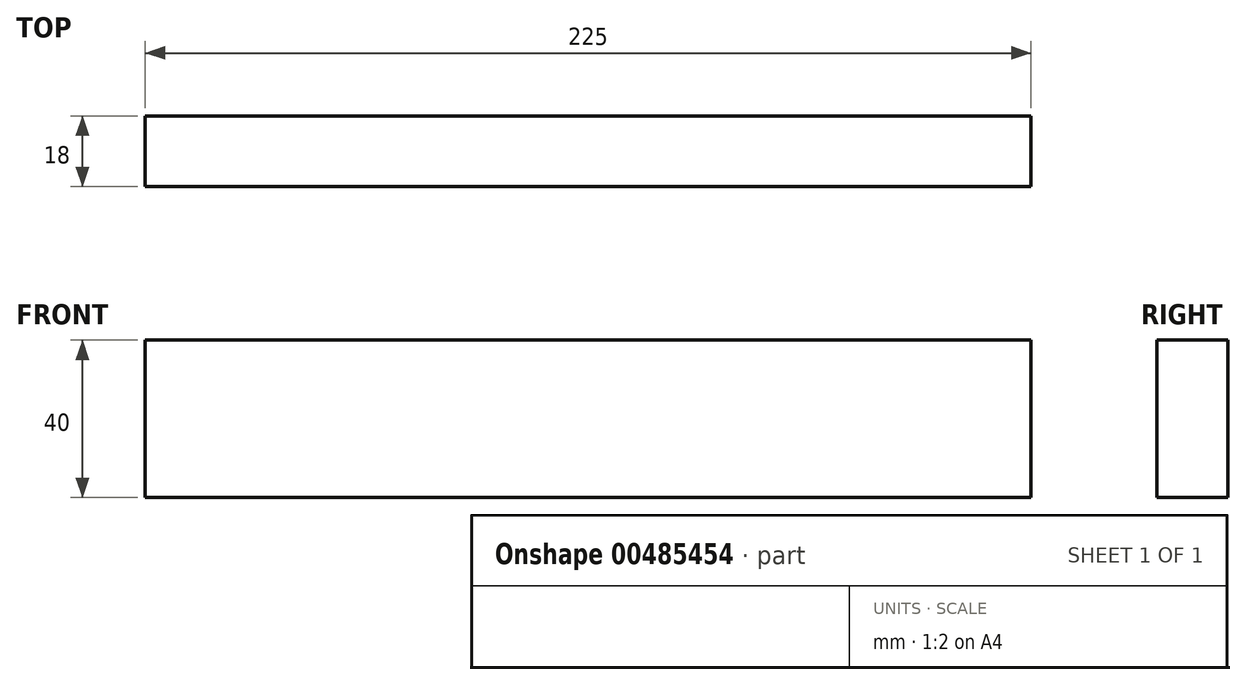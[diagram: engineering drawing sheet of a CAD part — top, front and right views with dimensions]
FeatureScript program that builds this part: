
annotation { "Feature Type Name" : "Feature", "Feature Type Description" : "" }
export const myFeature = defineFeature(function(context is Context, id is Id, definition is map)
    precondition{}
    {
        {
            var Q0;
            Q0=qCreatedBy(makeId("Right.planeOp"),FACE);
            var sketch = newSketch(context, id + "F0", { "sketchPlane" : qUnion([Q0])});
            skLineSegment(sketch, "E0.bottom", {"start": v(-9, 20) * mm, "end": v(9, 20) * mm});
            skLineSegment(sketch, "E0.top", {"start": v(-9, -20) * mm, "end": v(9, -20) * mm});
            skLineSegment(sketch, "E0.left", {"start": v(-9, 20) * mm, "end": v(-9, -20) * mm});
            skLineSegment(sketch, "E0.right", {"start": v(9, 20) * mm, "end": v(9, -20) * mm});
            skPoint(sketch, "E0.middle", {"position": v(0, 0) * mm});
            skSolve(sketch);
        }
        {
            var Q0;
            Q0=makeQuery(id+"F0.imprint","IMPRINT",FACE,{"disambiguationData":[TD([[makeQuery(id+"F0.imprint","IMPRINT",EDGE,{"derivedFrom":sQuery(id+"F0.wireOp",EDGE,"E0.bottom")}),-1.0]])]});
            extrude(context, id + "F1", {"entities" : qUnion([Q0]), "oppositeDirection" : true, "depth" : 225 * mm});
        }
    });
